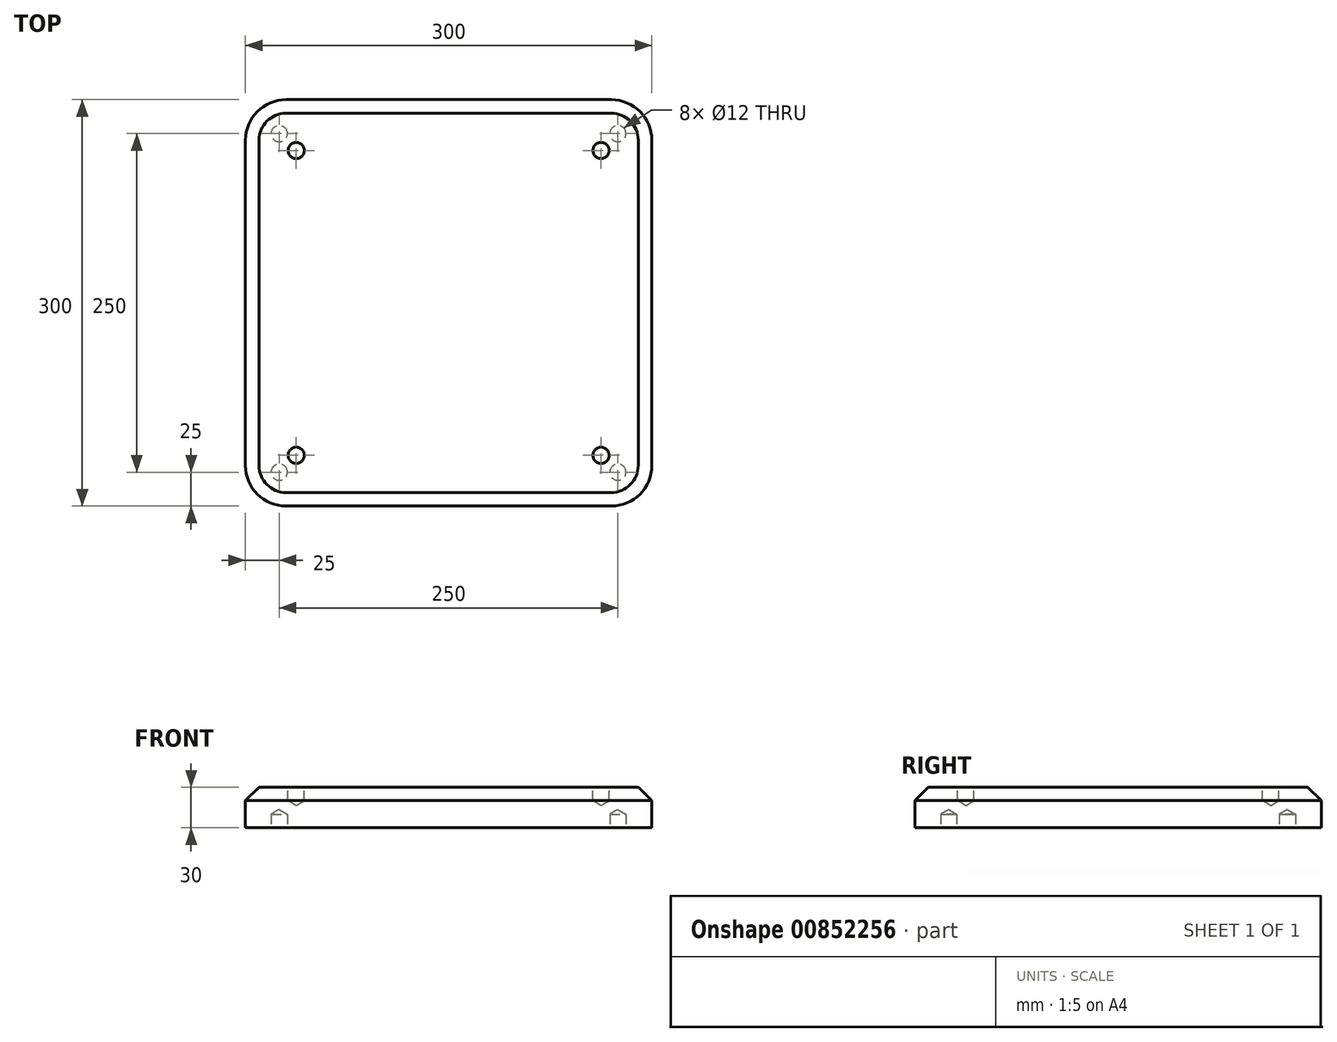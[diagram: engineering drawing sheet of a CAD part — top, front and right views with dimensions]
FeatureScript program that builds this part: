
annotation { "Feature Type Name" : "Feature", "Feature Type Description" : "" }
export const myFeature = defineFeature(function(context is Context, id is Id, definition is map)
    precondition{}
    {
        {
            var Q0;
            Q0=qCreatedBy(makeId("Top.planeOp"),FACE);
            var sketch = newSketch(context, id + "F0", { "sketchPlane" : qUnion([Q0])});
            skLineSegment(sketch, "E0.bottom", {"start": v(-120, 150) * mm, "end": v(120, 150) * mm});
            skLineSegment(sketch, "E0.top", {"start": v(-120, -150) * mm, "end": v(120, -150) * mm});
            skLineSegment(sketch, "E0.left", {"start": v(-150, 120) * mm, "end": v(-150, -120) * mm});
            skLineSegment(sketch, "E0.right", {"start": v(150, 120) * mm, "end": v(150, -120) * mm});
            skPoint(sketch, "E0.middle", {"position": v(0, 0) * mm});
            skPoint(sketch, "E1.visualSharp", {"position": v(-150, 150) * mm});
            skArc(sketch, "E1.filletArc", {"start": v(-120, 150) * mm, "mid": v(-141.21, 141.21) * mm, "end": v(-150, 120) * mm});
            skPoint(sketch, "E2.visualSharp", {"position": v(150, 150) * mm});
            skArc(sketch, "E2.filletArc", {"start": v(150, 120) * mm, "mid": v(141.21, 141.21) * mm, "end": v(120, 150) * mm});
            skPoint(sketch, "E3.visualSharp", {"position": v(150, -150) * mm});
            skArc(sketch, "E3.filletArc", {"start": v(120, -150) * mm, "mid": v(141.21, -141.21) * mm, "end": v(150, -120) * mm});
            skPoint(sketch, "E4.visualSharp", {"position": v(-150, -150) * mm});
            skArc(sketch, "E4.filletArc", {"start": v(-150, -120) * mm, "mid": v(-141.21, -141.21) * mm, "end": v(-120, -150) * mm});
            skSolve(sketch);
        }
        {
            var Q0;
            Q0 = qSketchRegion(id + "F0", true);
            extrude(context, id + "F1", {"entities" : qUnion([Q0]), "depth" : 30 * mm, "offsetDistance" : 25 * mm});
        }
        {
            var Q0;
            Q0=makeQuery(id+"F1.opExtrude","CAP_EDGE",EDGE,{"disambiguationData":[OSD([sQuery(id+"F0.wireOp",EDGE,"E0.left")])],"isStart":false});
            chamfer(context, id + "F2", {"entities" : qUnion([Q0]), "width" : 10 * mm, "tangentPropagation" : true});
        }
        {
            var Q0;
            Q0=makeQuery(id+"F1.opExtrude","CAP_FACE",FACE,{"disambiguationData":[OSD([sQuery(id+"F0.wireOp",EDGE,"E0.bottom"),sQuery(id+"F0.wireOp",EDGE,"E0.top"),sQuery(id+"F0.wireOp",EDGE,"E0.left"),sQuery(id+"F0.wireOp",EDGE,"E0.right"),sQuery(id+"F0.wireOp",EDGE,"E1.filletArc"),sQuery(id+"F0.wireOp",EDGE,"E2.filletArc"),sQuery(id+"F0.wireOp",EDGE,"E3.filletArc"),sQuery(id+"F0.wireOp",EDGE,"E4.filletArc")])],"isStart":false});
            var sketch = newSketch(context, id + "F3", { "sketchPlane" : qUnion([Q0])});
            skLineSegment(sketch, "E5.bottom", {"start": v(-112.5, 112.5) * mm, "end": v(112.5, 112.5) * mm, "construction": true});
            skLineSegment(sketch, "E5.top", {"start": v(-112.5, -112.5) * mm, "end": v(112.5, -112.5) * mm, "construction": true});
            skLineSegment(sketch, "E5.left", {"start": v(-112.5, 112.5) * mm, "end": v(-112.5, -112.5) * mm, "construction": true});
            skLineSegment(sketch, "E5.right", {"start": v(112.5, 112.5) * mm, "end": v(112.5, -112.5) * mm, "construction": true});
            skPoint(sketch, "E5.middle", {"position": v(0, 0) * mm});
            skSolve(sketch);
        }
        {
            var Q0;
            Q0=sQuery(id+"F3.wireOp",VERTEX,"E5.bottom.start");
            var Q1;
            Q1=sQuery(id+"F3.wireOp",VERTEX,"E5.top.start");
            var Q2;
            Q2=sQuery(id+"F3.wireOp",VERTEX,"E5.bottom.end");
            var Q3;
            Q3=sQuery(id+"F3.wireOp",VERTEX,"E5.top.end");
            var Q4;
            Q4=makeQuery(id+"F1.opExtrude","SWEPT_BODY",BODY,{"disambiguationData":[OSD([sQuery(id+"F0.wireOp",EDGE,"E0.bottom"),sQuery(id+"F0.wireOp",EDGE,"E0.top"),sQuery(id+"F0.wireOp",EDGE,"E0.left"),sQuery(id+"F0.wireOp",EDGE,"E0.right"),sQuery(id+"F0.wireOp",EDGE,"E1.filletArc"),sQuery(id+"F0.wireOp",EDGE,"E2.filletArc"),sQuery(id+"F0.wireOp",EDGE,"E3.filletArc"),sQuery(id+"F0.wireOp",EDGE,"E4.filletArc")])]});
            hole(context, id + "F4", {"style" : HoleStyle.SIMPLE, "endStyle" : HoleEndStyle.BLIND, "holeDiameter" : 12 * mm, "majorDiameter" : 5 * mm, "holeDepth" : 10 * mm, "isTappedThrough" : true, "tappedDepth" : 12 * mm, "tapClearance" : 3, "locations" : qUnion([Q0, Q1, Q2, Q3]), "scope" : qUnion([Q4])});
        }
        {
            var Q0;
            Q0=makeQuery(id+"F1.opExtrude","CAP_FACE",FACE,{"disambiguationData":[OSD([sQuery(id+"F0.wireOp",EDGE,"E0.bottom"),sQuery(id+"F0.wireOp",EDGE,"E0.top"),sQuery(id+"F0.wireOp",EDGE,"E0.left"),sQuery(id+"F0.wireOp",EDGE,"E0.right"),sQuery(id+"F0.wireOp",EDGE,"E1.filletArc"),sQuery(id+"F0.wireOp",EDGE,"E2.filletArc"),sQuery(id+"F0.wireOp",EDGE,"E3.filletArc"),sQuery(id+"F0.wireOp",EDGE,"E4.filletArc")])],"isStart":true});
            var sketch = newSketch(context, id + "F5", { "sketchPlane" : qUnion([Q0])});
            skLineSegment(sketch, "E6.bottom", {"start": v(-125, 125) * mm, "end": v(125, 125) * mm, "construction": true});
            skLineSegment(sketch, "E6.top", {"start": v(-125, -125) * mm, "end": v(125, -125) * mm, "construction": true});
            skLineSegment(sketch, "E6.left", {"start": v(-125, 125) * mm, "end": v(-125, -125) * mm, "construction": true});
            skLineSegment(sketch, "E6.right", {"start": v(125, 125) * mm, "end": v(125, -125) * mm, "construction": true});
            skPoint(sketch, "E6.middle", {"position": v(0, 0) * mm});
            skSolve(sketch);
        }
        {
            var Q0;
            Q0=sQuery(id+"F5.wireOp",VERTEX,"E6.bottom.start");
            var Q1;
            Q1=sQuery(id+"F5.wireOp",VERTEX,"E6.bottom.end");
            var Q2;
            Q2=sQuery(id+"F5.wireOp",VERTEX,"E6.top.end");
            var Q3;
            Q3=sQuery(id+"F5.wireOp",VERTEX,"E6.top.start");
            var Q4;
            Q4=makeQuery(id+"F1.opExtrude","SWEPT_BODY",BODY,{"disambiguationData":[OSD([sQuery(id+"F0.wireOp",EDGE,"E0.bottom"),sQuery(id+"F0.wireOp",EDGE,"E0.top"),sQuery(id+"F0.wireOp",EDGE,"E0.left"),sQuery(id+"F0.wireOp",EDGE,"E0.right"),sQuery(id+"F0.wireOp",EDGE,"E1.filletArc"),sQuery(id+"F0.wireOp",EDGE,"E2.filletArc"),sQuery(id+"F0.wireOp",EDGE,"E3.filletArc"),sQuery(id+"F0.wireOp",EDGE,"E4.filletArc")])]});
            hole(context, id + "F6", {"style" : HoleStyle.SIMPLE, "endStyle" : HoleEndStyle.BLIND, "holeDiameter" : 12 * mm, "majorDiameter" : 5 * mm, "holeDepth" : 10 * mm, "isTappedThrough" : true, "tappedDepth" : 12 * mm, "tapClearance" : 3, "locations" : qUnion([Q0, Q1, Q2, Q3]), "scope" : qUnion([Q4])});
        }
    });
